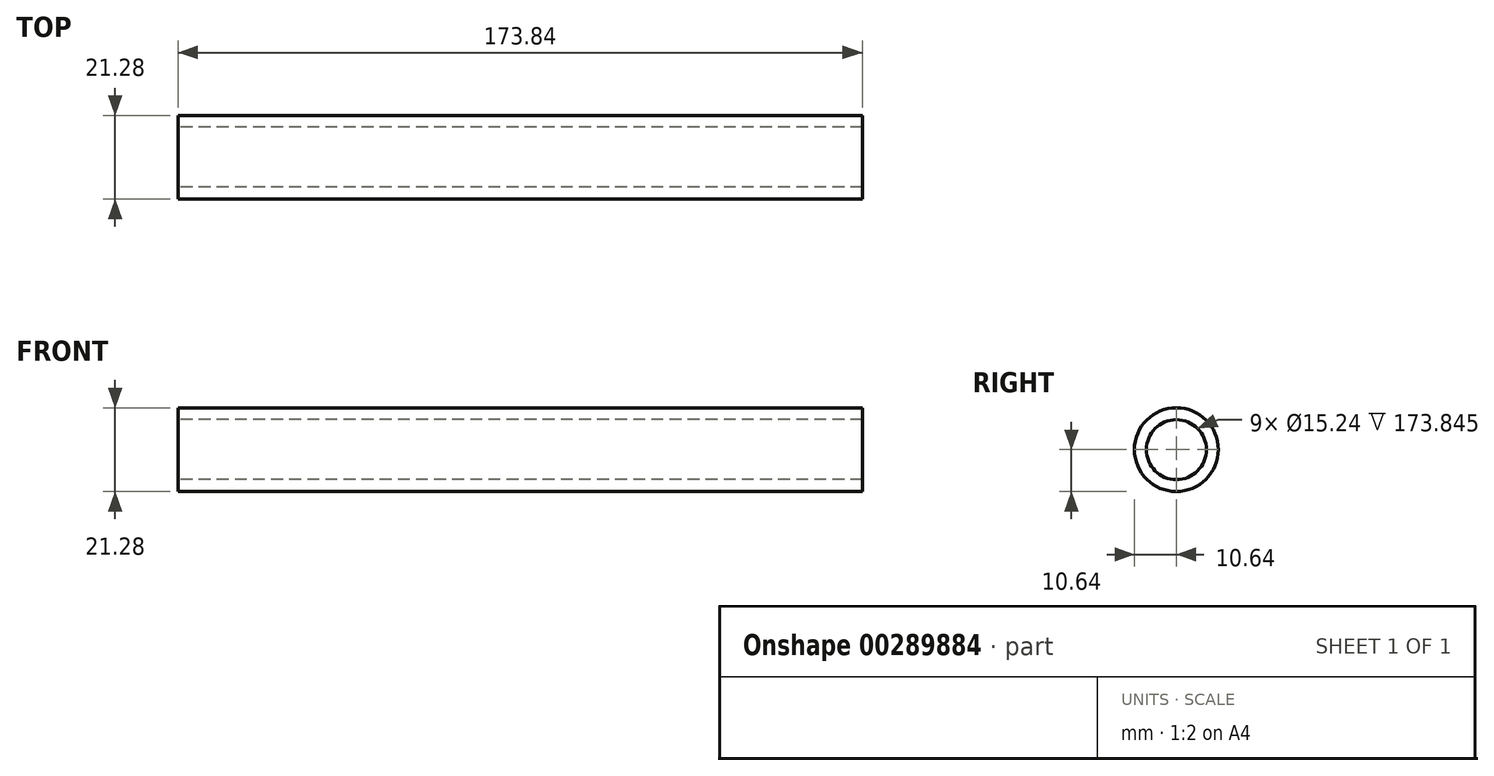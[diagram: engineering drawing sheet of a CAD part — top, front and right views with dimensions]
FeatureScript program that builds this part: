
annotation { "Feature Type Name" : "Feature", "Feature Type Description" : "" }
export const myFeature = defineFeature(function(context is Context, id is Id, definition is map)
    precondition{}
    {
        {
            var Q0;
            Q0=qCreatedBy(makeId("Right.planeOp"),FACE);
            var sketch = newSketch(context, id + "F0", { "sketchPlane" : qUnion([Q0])});
            skCircle(sketch, "E0", {"center": v(0, 0) * mm, "radius": 7.62 * mm});
            skCircle(sketch, "E1", {"center": v(0, 0) * mm, "radius": 10.64 * mm});
            skSolve(sketch);
        }
        {
            var Q0;
            Q0=makeQuery(id+"F0.imprint","IMPRINT",FACE,{"disambiguationData":[TD([[makeQuery(id+"F0.imprint","IMPRINT",EDGE,{"derivedFrom":sQuery(id+"F0.wireOp",EDGE,"E0")}),-1.0]])]});
            extrude(context, id + "F1", {"entities" : qUnion([Q0]), "endBound" : BoundingType.SYMMETRIC, "depth" : 203.2 * mm + 3 / 203.2 * mm - 33.53 * mm + 4.16 * mm});
        }
    });
